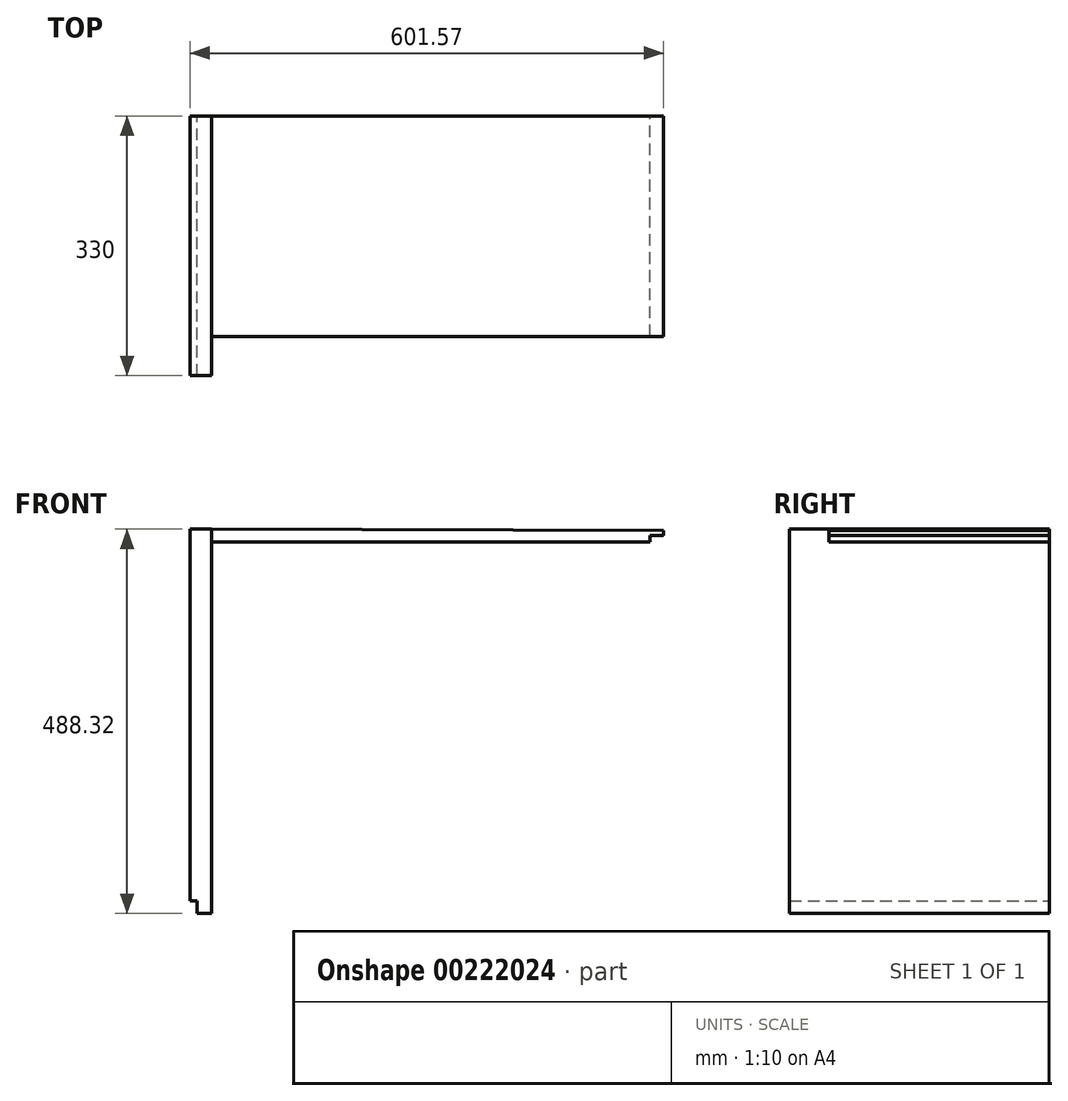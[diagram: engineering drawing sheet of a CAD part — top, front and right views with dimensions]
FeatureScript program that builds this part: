
annotation { "Feature Type Name" : "Feature", "Feature Type Description" : "" }
export const myFeature = defineFeature(function(context is Context, id is Id, definition is map)
    precondition{}
    {
        {
            var Q0;
            Q0=qCreatedBy(makeId("Front.planeOp"),FACE);
            var sketch = newSketch(context, id + "F0", { "sketchPlane" : qUnion([Q0])});
            skLineSegment(sketch, "E0", {"start": v(-166.64, 163.91) * mm, "end": v(-166.64, 147.4) * mm});
            skLineSegment(sketch, "E1", {"start": v(-166.64, 147.4) * mm, "end": v(390.46, 147.4) * mm});
            skLineSegment(sketch, "E2", {"start": v(390.46, 147.4) * mm, "end": v(390.46, 155.65) * mm});
            skLineSegment(sketch, "E3", {"start": v(407.73, 155.65) * mm, "end": v(407.73, 162.41) * mm});
            skLineSegment(sketch, "E4", {"start": v(407.73, 162.41) * mm, "end": v(-166.64, 163.91) * mm});
            skLineSegment(sketch, "E5", {"start": v(390.46, 155.65) * mm, "end": v(407.73, 155.65) * mm});
            skLineSegment(sketch, "E6", {"start": v(-166.64, 163.91) * mm, "end": v(-193.84, 163.91) * mm});
            skLineSegment(sketch, "E7", {"start": v(-193.84, 163.91) * mm, "end": v(-193.84, -308) * mm});
            skLineSegment(sketch, "E8", {"start": v(-193.84, -308) * mm, "end": v(-185.2, -308) * mm});
            skLineSegment(sketch, "E9", {"start": v(-185.2, -308) * mm, "end": v(-185.2, -324.4) * mm});
            skLineSegment(sketch, "E10", {"start": v(-185.2, -324.4) * mm, "end": v(-166.64, -324.4) * mm});
            skLineSegment(sketch, "E11", {"start": v(-166.64, -324.4) * mm, "end": v(-166.64, 163.91) * mm});
            skSolve(sketch);
        }
        {
            var Q0;
            Q0=makeQuery(id+"F0.imprint","IMPRINT",FACE,{"disambiguationData":[TD([[makeQuery(id+"F0.imprint","IMPRINT",EDGE,{"derivedFrom":sQuery(id+"F0.wireOp",EDGE,"E0")}),1.0]])]});
            extrude(context, id + "F1", {"entities" : qUnion([Q0]), "depth" : 280 * mm});
        }
        {
            var Q0;
            {var subQ0=sQuery(id+"F0.wireOp",EDGE,"E6");Q0=makeQuery(id+"F0.imprint","IMPRINT",FACE,{"disambiguationData":[TD([[makeQuery(id+"F0.imprint","IMPRINT",EDGE,{"derivedFrom":subQ0}),1.0]])]});}
            extrude(context, id + "F2", {"entities" : qUnion([Q0]), "depth" : 330 * mm});
        }
    });
